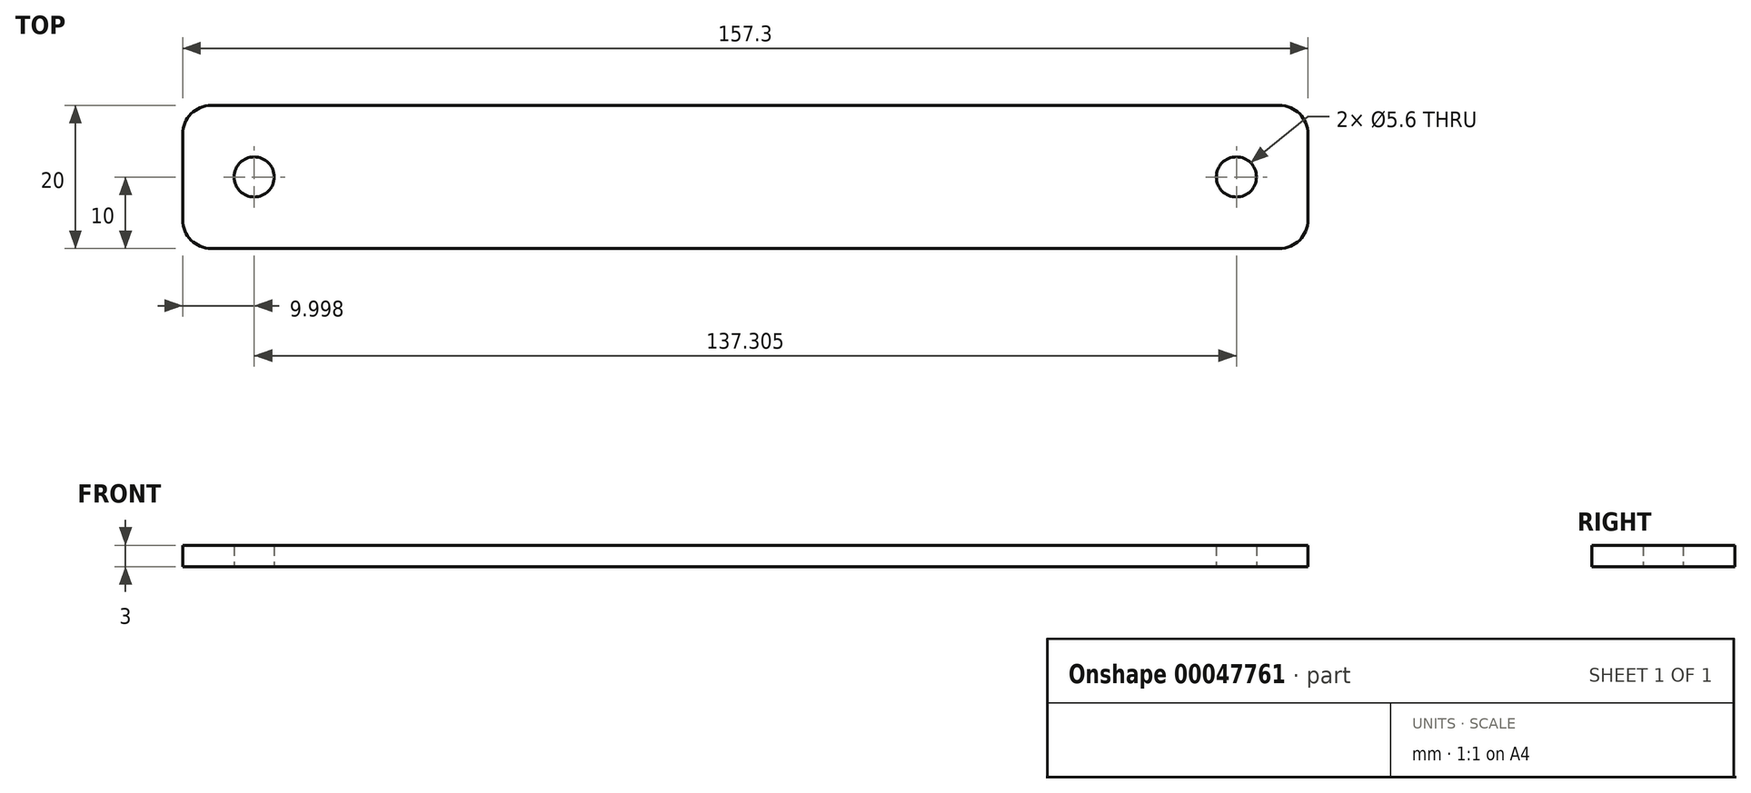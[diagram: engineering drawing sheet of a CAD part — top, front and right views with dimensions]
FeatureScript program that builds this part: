
annotation { "Feature Type Name" : "Feature", "Feature Type Description" : "" }
export const myFeature = defineFeature(function(context is Context, id is Id, definition is map)
    precondition{}
    {
        {
            var Q0;
            Q0=qCreatedBy(makeId("Top.planeOp"),FACE);
            var sketch = newSketch(context, id + "F0", { "sketchPlane" : qUnion([Q0])});
            skLineSegment(sketch, "E0.bottom", {"start": v(-74.65, 10) * mm, "end": v(74.65, 10) * mm});
            skLineSegment(sketch, "E0.top", {"start": v(-74.65, -10) * mm, "end": v(74.65, -10) * mm});
            skLineSegment(sketch, "E0.left", {"start": v(-78.65, 6) * mm, "end": v(-78.65, -6) * mm});
            skLineSegment(sketch, "E0.right", {"start": v(78.65, 6) * mm, "end": v(78.65, -6) * mm});
            skPoint(sketch, "E0.middle", {"position": v(0, 0) * mm});
            skCircle(sketch, "E1", {"center": v(-68.65, 0) * mm, "radius": 2.8 * mm});
            skPoint(sketch, "E1.centerSnap0", {"position": v(-78.65, 0) * mm});
            skCircle(sketch, "E2", {"center": v(68.65, 0) * mm, "radius": 2.8 * mm});
            skPoint(sketch, "E3.visualSharp", {"position": v(-78.65, 10) * mm});
            skArc(sketch, "E3.filletArc", {"start": v(-74.65, 10) * mm, "mid": v(-77.48, 8.83) * mm, "end": v(-78.65, 6) * mm});
            skPoint(sketch, "E4.visualSharp", {"position": v(-78.65, -10) * mm});
            skArc(sketch, "E4.filletArc", {"start": v(-78.65, -6) * mm, "mid": v(-77.48, -8.83) * mm, "end": v(-74.65, -10) * mm});
            skPoint(sketch, "E5.visualSharp", {"position": v(78.65, 10) * mm});
            skArc(sketch, "E5.filletArc", {"start": v(78.65, 6) * mm, "mid": v(77.48, 8.83) * mm, "end": v(74.65, 10) * mm});
            skPoint(sketch, "E6.visualSharp", {"position": v(78.65, -10) * mm});
            skArc(sketch, "E6.filletArc", {"start": v(74.65, -10) * mm, "mid": v(77.48, -8.83) * mm, "end": v(78.65, -6) * mm});
            skSolve(sketch);
        }
        {
            var Q0;
            Q0=makeQuery(id+"F0.imprint","IMPRINT",FACE,{"disambiguationData":[TD([[makeQuery(id+"F0.imprint","IMPRINT",EDGE,{"derivedFrom":sQuery(id+"F0.wireOp",EDGE,"E0.bottom")}),-1.0]])]});
            extrude(context, id + "F1", {"entities" : qUnion([Q0]), "depth" : 3 * mm});
        }
    });
